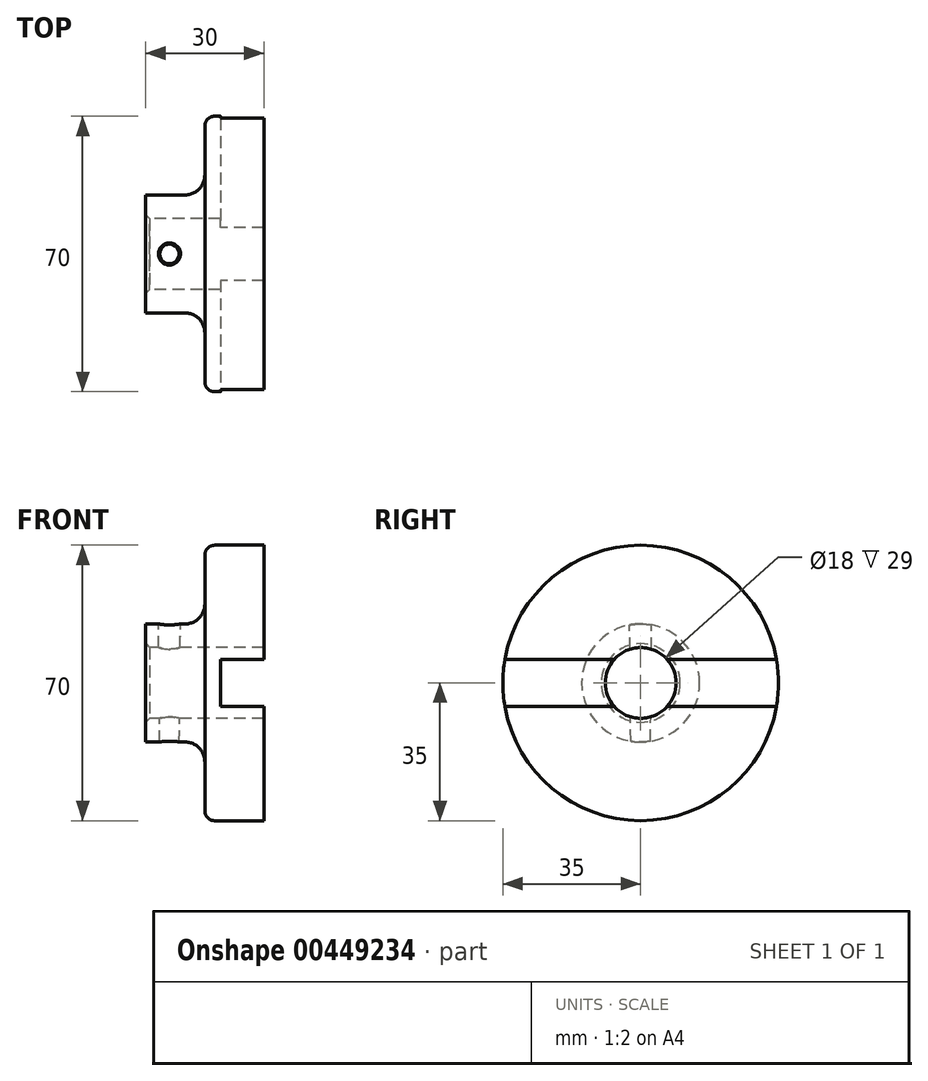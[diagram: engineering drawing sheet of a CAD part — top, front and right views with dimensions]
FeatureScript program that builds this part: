
annotation { "Feature Type Name" : "Feature", "Feature Type Description" : "" }
export const myFeature = defineFeature(function(context is Context, id is Id, definition is map)
    precondition{}
    {
        {
            var Q0;
            Q0=qCreatedBy(makeId("Front.planeOp"),FACE);
            var sketch = newSketch(context, id + "F0", { "sketchPlane" : qUnion([Q0])});
            skLineSegment(sketch, "E0", {"start": v(0, 0) * mm, "end": v(26.6, 0) * mm, "construction": true});
            skLineSegment(sketch, "E1", {"start": v(0, 9) * mm, "end": v(0, 15) * mm});
            skLineSegment(sketch, "E2", {"start": v(0, 15) * mm, "end": v(10, 15) * mm});
            skLineSegment(sketch, "E3", {"start": v(15, 20) * mm, "end": v(15, 32.5) * mm});
            skLineSegment(sketch, "E4", {"start": v(17.5, 35) * mm, "end": v(30, 35) * mm});
            skLineSegment(sketch, "E5", {"start": v(30, 35) * mm, "end": v(30, 9) * mm});
            skLineSegment(sketch, "E6", {"start": v(30, 9) * mm, "end": v(0, 9) * mm});
            skPoint(sketch, "E7.visualSharp", {"position": v(15, 15) * mm});
            skArc(sketch, "E7.filletArc", {"start": v(10, 15) * mm, "mid": v(13.54, 16.46) * mm, "end": v(15, 20) * mm});
            skPoint(sketch, "E8.visualSharp", {"position": v(15, 35) * mm});
            skArc(sketch, "E8.filletArc", {"start": v(17.5, 35) * mm, "mid": v(15.73, 34.27) * mm, "end": v(15, 32.5) * mm});
            skSolve(sketch);
        }
        {
            var Q0;
            Q0 = qSketchRegion(id + "F0", true);
            var Q1;
            Q1=sQuery(id+"F0.wireOp",EDGE,"E0");
            revolve(context, id + "F1", {"entities" : qUnion([Q0]), "axis" : qUnion([Q1]), "revolveType" : RevolveType.FULL});
        }
        {
            var Q0;
            Q0=qCreatedBy(makeId("Front.planeOp"),FACE);
            var sketch = newSketch(context, id + "F2", { "sketchPlane" : qUnion([Q0])});
            skLineSegment(sketch, "E9.bottom", {"start": v(19, -6) * mm, "end": v(30, -6) * mm});
            skLineSegment(sketch, "E9.top", {"start": v(19, 6) * mm, "end": v(30, 6) * mm});
            skLineSegment(sketch, "E9.left", {"start": v(19, -6) * mm, "end": v(19, 6) * mm});
            skLineSegment(sketch, "E9.right", {"start": v(30, -6) * mm, "end": v(30, 6) * mm});
            skLineSegment(sketch, "E10", {"start": v(0, 0) * mm, "end": v(6.58, 0) * mm, "construction": true});
            skSolve(sketch);
        }
        {
            var Q0;
            Q0 = qSketchRegion(id + "F2", true);
            extrude(context, id + "F3", {"entities" : qUnion([Q0]), "operationType" : NewBodyOperationType.REMOVE, "oppositeDirection" : true, "depth" : 80 * mm, "symmetric" : true});
        }
        {
            var Q0;
            Q0=makeQuery(id+"F1.opRevolve","SWEPT_EDGE",EDGE,{"disambiguationData":[OSD([sQuery(id+"F0.wireOp",EDGE,"E1"),sQuery(id+"F0.wireOp",EDGE,"E6")])]});
            var Q1;
            Q1=makeQuery(id+"F3.boolean.opBoolean","COPY",EDGE,{"disambiguationData":[OD(0.0)],"derivedFrom":makeQuery(id+"F3.opExtrude","SWEPT_EDGE",EDGE,{"disambiguationData":[OSD([sQuery(id+"F2.wireOp",EDGE,"E9.top"),sQuery(id+"F2.wireOp",EDGE,"E9.right")])]})});
            var Q2;
            Q2=makeQuery(id+"F3.boolean.opBoolean","COPY",EDGE,{"disambiguationData":[OD(1.0)],"derivedFrom":makeQuery(id+"F3.opExtrude","SWEPT_EDGE",EDGE,{"disambiguationData":[OSD([sQuery(id+"F2.wireOp",EDGE,"E9.top"),sQuery(id+"F2.wireOp",EDGE,"E9.right")])]})});
            var Q3;
            Q3=makeQuery(id+"F3.boolean.opBoolean","COPY",EDGE,{"disambiguationData":[OD(1.0)],"derivedFrom":makeQuery(id+"F3.opExtrude","SWEPT_EDGE",EDGE,{"disambiguationData":[OSD([sQuery(id+"F2.wireOp",EDGE,"E9.bottom"),sQuery(id+"F2.wireOp",EDGE,"E9.right")])]})});
            var Q4;
            Q4=makeQuery(id+"F3.boolean.opBoolean","COPY",EDGE,{"disambiguationData":[OD(0.0)],"derivedFrom":makeQuery(id+"F3.opExtrude","SWEPT_EDGE",EDGE,{"disambiguationData":[OSD([sQuery(id+"F2.wireOp",EDGE,"E9.bottom"),sQuery(id+"F2.wireOp",EDGE,"E9.right")])]})});
            chamfer(context, id + "F4", {"entities" : qUnion([Q0, Q1, Q2, Q3, Q4]), "width" : 1 * mm, "tangentPropagation" : true});
        }
        {
            var Q0;
            Q0=qCreatedBy(makeId("Front.planeOp"),FACE);
            var sketch = newSketch(context, id + "F5", { "sketchPlane" : qUnion([Q0])});
            skLineSegment(sketch, "E11", {"start": v(6, 16.93) * mm, "end": v(6, -17.7) * mm, "construction": true});
            skLineSegment(sketch, "E12", {"start": v(8.5, -15) * mm, "end": v(6, -15) * mm});
            skLineSegment(sketch, "E13", {"start": v(8.5, -15) * mm, "end": v(8.8, 15) * mm});
            skLineSegment(sketch, "E14", {"start": v(6, 15) * mm, "end": v(8.8, 15) * mm});
            skPoint(sketch, "E15.orphan", {"position": v(9.5, 85) * mm});
            skLineSegment(sketch, "E16", {"start": v(6, -15) * mm, "end": v(6, 15) * mm});
            skLineSegment(sketch, "E17", {"start": v(8.5, -15) * mm, "end": v(8.5, -15.64) * mm});
            skLineSegment(sketch, "E18", {"start": v(8.5, -15.64) * mm, "end": v(6, -15.64) * mm});
            skLineSegment(sketch, "E19", {"start": v(6, -15.64) * mm, "end": v(6, -15) * mm});
            skLineSegment(sketch, "E20", {"start": v(8.8, 15) * mm, "end": v(8.8, 15.99) * mm});
            skLineSegment(sketch, "E21", {"start": v(8.8, 15.99) * mm, "end": v(6, 15.99) * mm});
            skLineSegment(sketch, "E22", {"start": v(6, 15.99) * mm, "end": v(6, 15) * mm});
            skSolve(sketch);
        }
        {
            var Q0;
            Q0 = qSketchRegion(id + "F5", true);
            var Q1;
            Q1=sQuery(id+"F5.wireOp",EDGE,"E11");
            revolve(context, id + "F6", {"operationType" : NewBodyOperationType.REMOVE, "entities" : qUnion([Q0]), "axis" : qUnion([Q1]), "revolveType" : RevolveType.FULL, "oppositeDirection" : true});
        }
    });
